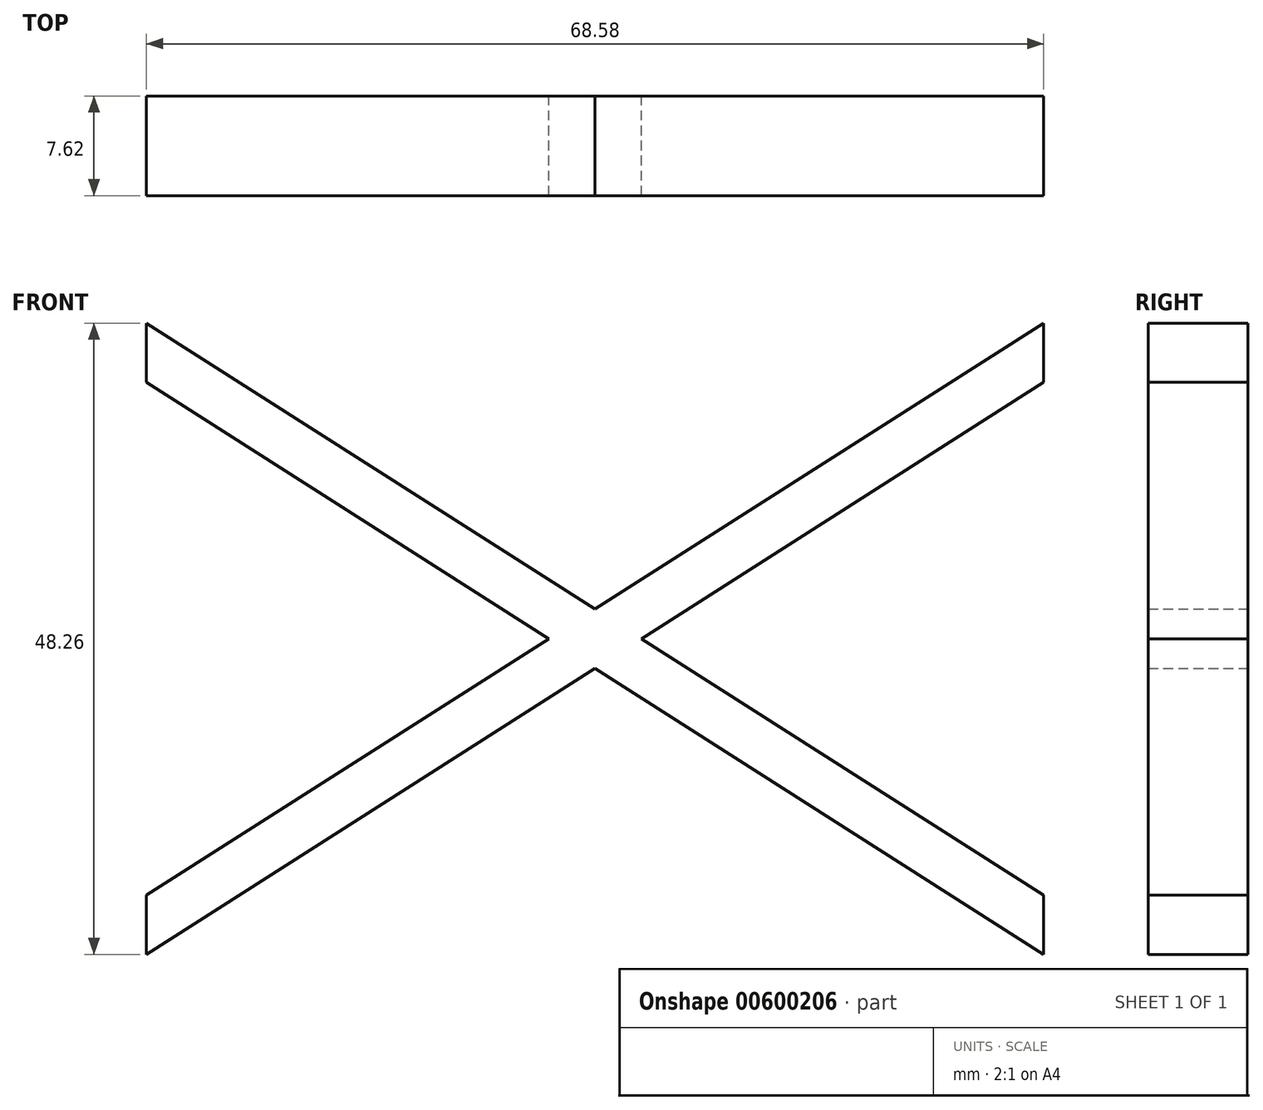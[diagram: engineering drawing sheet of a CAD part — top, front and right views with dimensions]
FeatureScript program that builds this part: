
annotation { "Feature Type Name" : "Feature", "Feature Type Description" : "" }
export const myFeature = defineFeature(function(context is Context, id is Id, definition is map)
    precondition{}
    {
        {
            var Q0;
            Q0=qCreatedBy(makeId("Front.planeOp"),FACE);
            var sketch = newSketch(context, id + "F0", { "sketchPlane" : qUnion([Q0])});
            skLineSegment(sketch, "E0", {"start": v(0, 0) * mm, "end": v(34.29, 21.87) * mm});
            skLineSegment(sketch, "E1", {"start": v(34.3, 21.87) * mm, "end": v(68.58, 0) * mm});
            skLineSegment(sketch, "E2", {"start": v(68.58, 0) * mm, "end": v(68.58, 4.52) * mm});
            skLineSegment(sketch, "E3", {"start": v(68.58, 4.52) * mm, "end": v(37.83, 24.13) * mm});
            skLineSegment(sketch, "E4", {"start": v(37.83, 24.13) * mm, "end": v(68.58, 43.74) * mm});
            skLineSegment(sketch, "E5", {"start": v(68.58, 43.74) * mm, "end": v(68.58, 48.26) * mm});
            skLineSegment(sketch, "E6", {"start": v(68.58, 48.26) * mm, "end": v(34.3, 26.39) * mm});
            skLineSegment(sketch, "E7", {"start": v(34.3, 26.39) * mm, "end": v(0, 48.26) * mm});
            skLineSegment(sketch, "E8", {"start": v(0, 48.26) * mm, "end": v(0, 43.74) * mm});
            skLineSegment(sketch, "E9", {"start": v(0, 43.74) * mm, "end": v(30.75, 24.13) * mm});
            skLineSegment(sketch, "E10", {"start": v(30.75, 24.13) * mm, "end": v(0, 4.52) * mm});
            skLineSegment(sketch, "E11", {"start": v(0, 4.52) * mm, "end": v(0, 0) * mm});
            skSolve(sketch);
        }
        {
            var Q0;
            Q0 = qSketchRegion(id + "F0", true);
            extrude(context, id + "F1", {"entities" : qUnion([Q0]), "depth" : 7.62 * mm, "offsetDistance" : 25.4 * mm});
        }
    });
